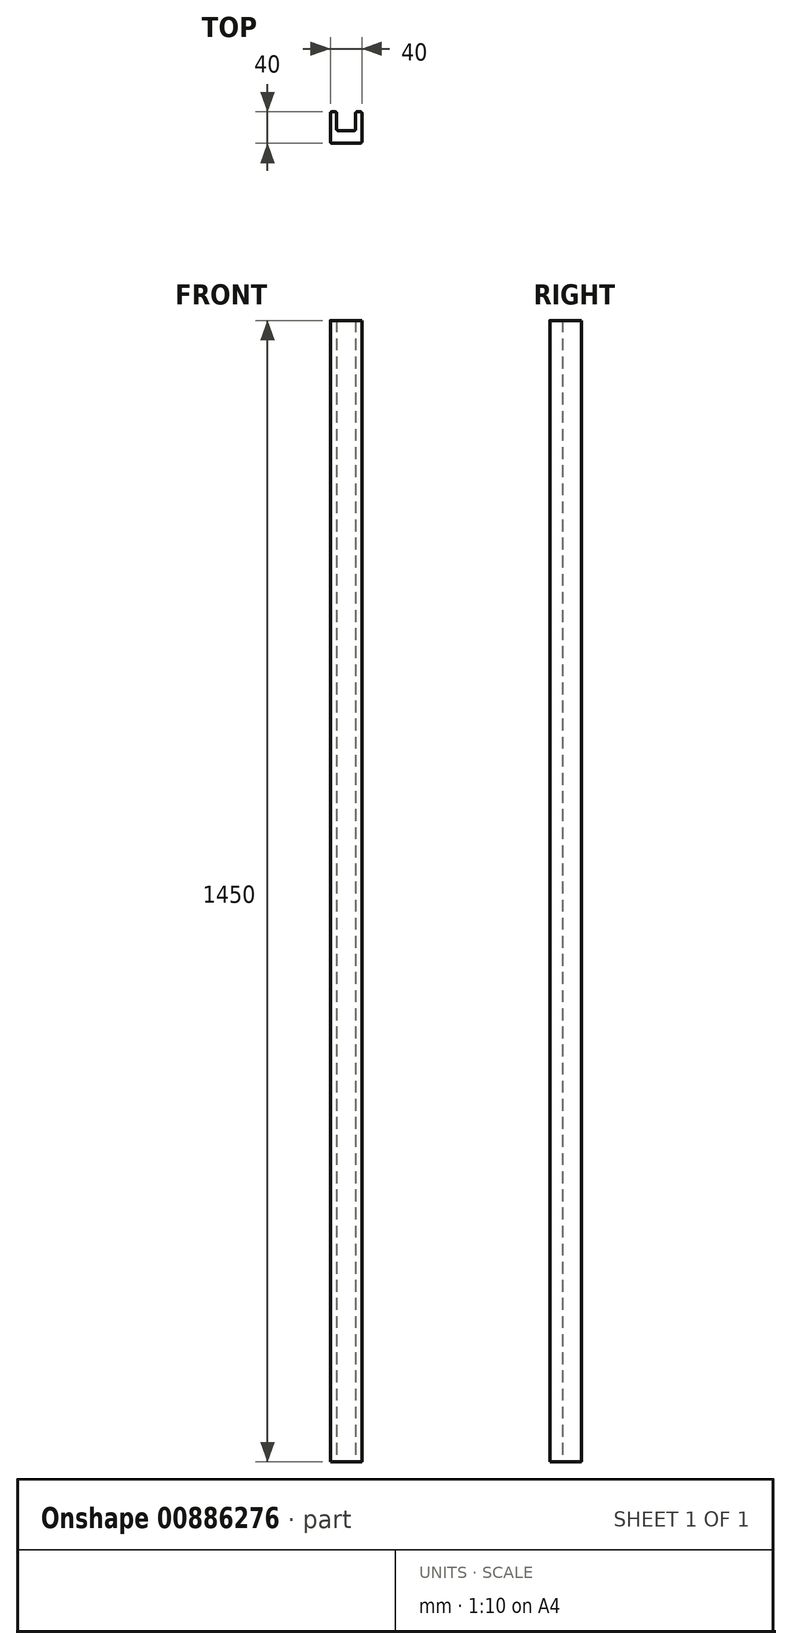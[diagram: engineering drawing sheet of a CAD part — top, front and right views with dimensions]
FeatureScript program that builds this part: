
annotation { "Feature Type Name" : "Feature", "Feature Type Description" : "" }
export const myFeature = defineFeature(function(context is Context, id is Id, definition is map)
    precondition{}
    {
        {
            var Q0;
            Q0=qCreatedBy(makeId("Top.planeOp"),FACE);
            var sketch = newSketch(context, id + "F0", { "sketchPlane" : qUnion([Q0])});
            skLineSegment(sketch, "E0.bottom", {"start": v(-16.77, 24) * mm, "end": v(-12.77, 24) * mm});
            skLineSegment(sketch, "E0.top", {"start": v(-16.77, -16) * mm, "end": v(19.23, -16) * mm});
            skLineSegment(sketch, "E0.left", {"start": v(-18.77, 22) * mm, "end": v(-18.77, -14) * mm});
            skLineSegment(sketch, "E0.right", {"start": v(21.23, 22) * mm, "end": v(21.23, -14) * mm});
            skPoint(sketch, "E0.middle", {"position": v(1.23, 4) * mm});
            skLineSegment(sketch, "E1", {"start": v(-10.77, 22) * mm, "end": v(-10.77, 2) * mm});
            skLineSegment(sketch, "E2", {"start": v(-8.77, 0) * mm, "end": v(11.23, 0) * mm});
            skLineSegment(sketch, "E3", {"start": v(13.23, 2) * mm, "end": v(13.23, 22) * mm});
            skLineSegment(sketch, "E4.trimOffspring", {"start": v(15.23, 24) * mm, "end": v(19.23, 24) * mm});
            skPoint(sketch, "E5.visualSharp", {"position": v(-18.77, 24) * mm});
            skArc(sketch, "E5.filletArc", {"start": v(-16.77, 24) * mm, "mid": v(-18.18, 23.41) * mm, "end": v(-18.77, 22) * mm});
            skPoint(sketch, "E6.visualSharp", {"position": v(-18.77, -16) * mm});
            skArc(sketch, "E6.filletArc", {"start": v(-18.77, -14) * mm, "mid": v(-18.18, -15.41) * mm, "end": v(-16.77, -16) * mm});
            skPoint(sketch, "E7.visualSharp", {"position": v(21.23, -16) * mm});
            skArc(sketch, "E7.filletArc", {"start": v(19.23, -16) * mm, "mid": v(20.65, -15.41) * mm, "end": v(21.23, -14) * mm});
            skPoint(sketch, "E8.visualSharp", {"position": v(-10.77, 0) * mm});
            skArc(sketch, "E8.filletArc", {"start": v(-10.77, 2) * mm, "mid": v(-10.18, 0.59) * mm, "end": v(-8.77, 0) * mm});
            skPoint(sketch, "E9.visualSharp", {"position": v(-10.77, 24) * mm});
            skArc(sketch, "E9.filletArc", {"start": v(-10.77, 22) * mm, "mid": v(-11.35, 23.41) * mm, "end": v(-12.77, 24) * mm});
            skPoint(sketch, "E10.visualSharp", {"position": v(13.23, 24) * mm});
            skArc(sketch, "E10.filletArc", {"start": v(15.23, 24) * mm, "mid": v(13.82, 23.41) * mm, "end": v(13.23, 22) * mm});
            skPoint(sketch, "E11.visualSharp", {"position": v(13.23, 0) * mm});
            skArc(sketch, "E11.filletArc", {"start": v(11.23, 0) * mm, "mid": v(12.65, 0.59) * mm, "end": v(13.23, 2) * mm});
            skPoint(sketch, "E12.visualSharp", {"position": v(21.23, 24) * mm});
            skArc(sketch, "E12.filletArc", {"start": v(21.23, 22) * mm, "mid": v(20.65, 23.41) * mm, "end": v(19.23, 24) * mm});
            skSolve(sketch);
        }
        {
            var Q0;
            Q0=makeQuery(id+"F0.imprint","IMPRINT",FACE,{"disambiguationData":[TD([[makeQuery(id+"F0.imprint","IMPRINT",EDGE,{"derivedFrom":sQuery(id+"F0.wireOp",EDGE,"E0.bottom")}),-1.0]])]});
            extrude(context, id + "F1", {"entities" : qUnion([Q0]), "depth" : 1450 * mm, "offsetDistance" : 25 * mm});
        }
    });
